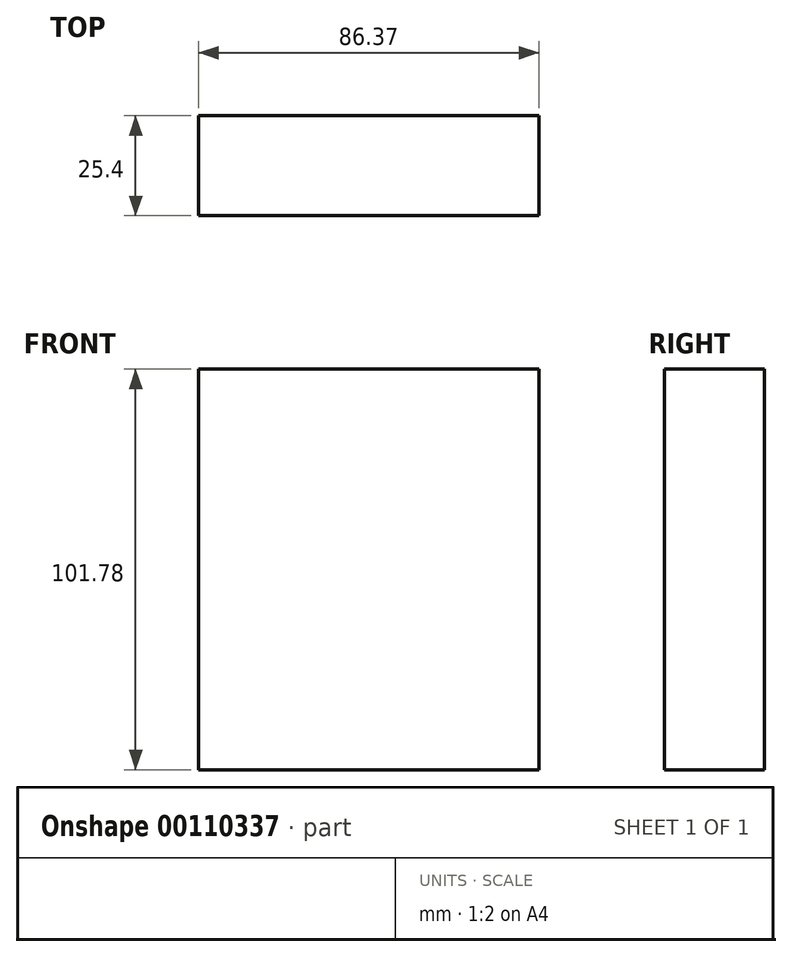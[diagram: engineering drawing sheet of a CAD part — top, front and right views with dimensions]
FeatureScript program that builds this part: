
annotation { "Feature Type Name" : "Feature", "Feature Type Description" : "" }
export const myFeature = defineFeature(function(context is Context, id is Id, definition is map)
    precondition{}
    {
        {
            var Q0;
            Q0=qCreatedBy(makeId("Front.planeOp"),FACE);
            var sketch = newSketch(context, id + "F0", { "sketchPlane" : qUnion([Q0])});
            skLineSegment(sketch, "E0.bottom", {"start": v(-41.53, 56.3) * mm, "end": v(44.84, 56.3) * mm});
            skLineSegment(sketch, "E0.top", {"start": v(-41.53, -45.47) * mm, "end": v(44.84, -45.47) * mm});
            skLineSegment(sketch, "E0.left", {"start": v(-41.53, 56.3) * mm, "end": v(-41.53, -45.47) * mm});
            skLineSegment(sketch, "E0.right", {"start": v(44.84, 56.3) * mm, "end": v(44.84, -45.47) * mm});
            skSolve(sketch);
        }
        {
            var Q0;
            Q0=makeQuery(id+"F0.imprint","IMPRINT",FACE,{"disambiguationData":[TD([[makeQuery(id+"F0.imprint","IMPRINT",EDGE,{"derivedFrom":sQuery(id+"F0.wireOp",EDGE,"E0.bottom")}),-1.0]])]});
            extrude(context, id + "F1", {"entities" : qUnion([Q0]), "depth" : 25.4 * mm});
        }
    });
